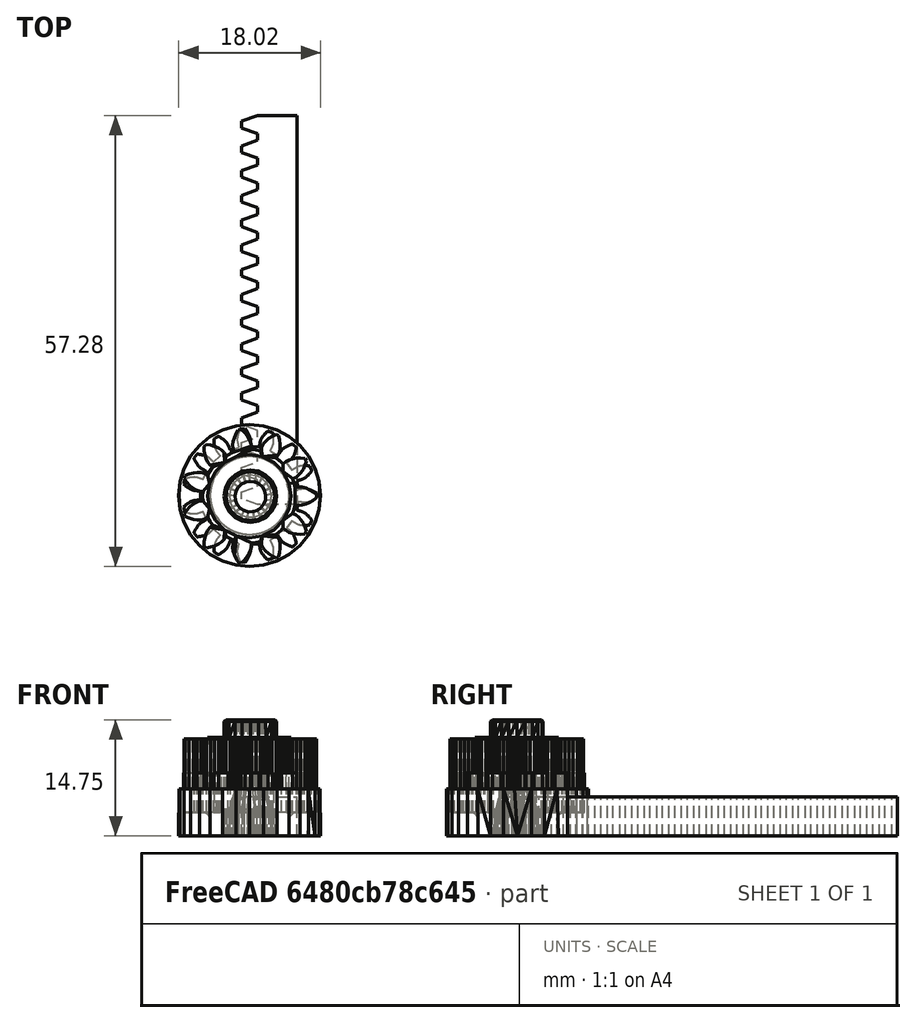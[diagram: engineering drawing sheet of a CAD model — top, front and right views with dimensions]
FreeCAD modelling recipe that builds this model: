
FCSTD DOCUMENT  (FreeCAD 0.16R5653 (Git))
Label: pinon para enfocador
License: All rights reserved
LicenseURL: http://en.wikipedia.org/wiki/All_rights_reserved
objects: Part::Feature×3, Part::Cylinder×3, Part::Cut×3, Part::FeaturePython×2, Mesh::Feature×1, Part::MultiFuse×1, Part::Fillet×1
note: 13 computed .brp shape members not serialized (recipe doc carries the construction recipe); baked Part::Feature solids carry a one-line shape summary decoded from their .brp

FEATURE [Part::FeaturePython] involute_rack  # WARN: FeaturePython — macro-defined, semantics opaque (R4)
  alpha = 20
  height = 5
  module = 1
  teeth = 15
  thickness = 5
FEATURE [Part::FeaturePython] involute_gear  # WARN: FeaturePython — macro-defined, semantics opaque (R4)
  Placement = pos=(0,0,3) rot=(0,0,1;0rad)
  alpha = 20
  backlash = 0
  beta = 0
  clearence = 0.25
  height = 5
  module = 1
  numpoints = 6
  shift = 0
  simple = false
  teeth = 15
  undercut = false
FEATURE [Mesh::Feature] inMoov_Wrist_StdSrvMnt_v3
FEATURE [Part::Feature] inMoov_Wrist_StdSrvMnt_v3001
  shape: bbox 18.01 x 18.02 x 14.75 mm, 1628 faces, 0 solids (baked)
FEATURE [Part::Feature] inMoov_Wrist_StdSrvMnt_v3001_solid  label="inMoov_Wrist_StdSrvMnt_v3001 (Solid)"
  shape: bbox 18.01 x 18.02 x 14.75 mm, 1628 faces (baked)
FEATURE [Part::Feature] inMoov_Wrist_StdSrvMnt_v3001_solid001  label="inMoov_Wrist_StdSrvMnt_v3001 (Solid)001"
  shape: bbox 18.01 x 18.02 x 14.75 mm, 908 faces (baked)
FEATURE [Part::Cylinder] Cylinder
  Angle = 360
  Height = 12
  Placement = pos=(0,0,4) rot=(0,0,1;0rad)
  Radius = 10
FEATURE [Part::Cut] Cut
  Base = -> inMoov_Wrist_StdSrvMnt_v3001_solid001
  Tool = -> Cylinder
FEATURE [Part::Cylinder] Cylinder001
  Angle = 360
  Height = 5
  Radius = 11
FEATURE [Part::Cylinder] Cylinder002
  Angle = 360
  Height = 5
  Radius = 5
FEATURE [Part::Cut] Cut001
  Base = -> Cylinder001
  Tool = -> Cylinder002
FEATURE [Part::Cut] Cut002
  Base = -> Cut
  Tool = -> Cut001
FEATURE [Part::MultiFuse] Fusion
  Shapes = -> [involute_gear,Cut002]
FEATURE [Part::Fillet] Fillet
  Base = -> Fusion
  Edges = 1 edges r=1: [Edge98]
